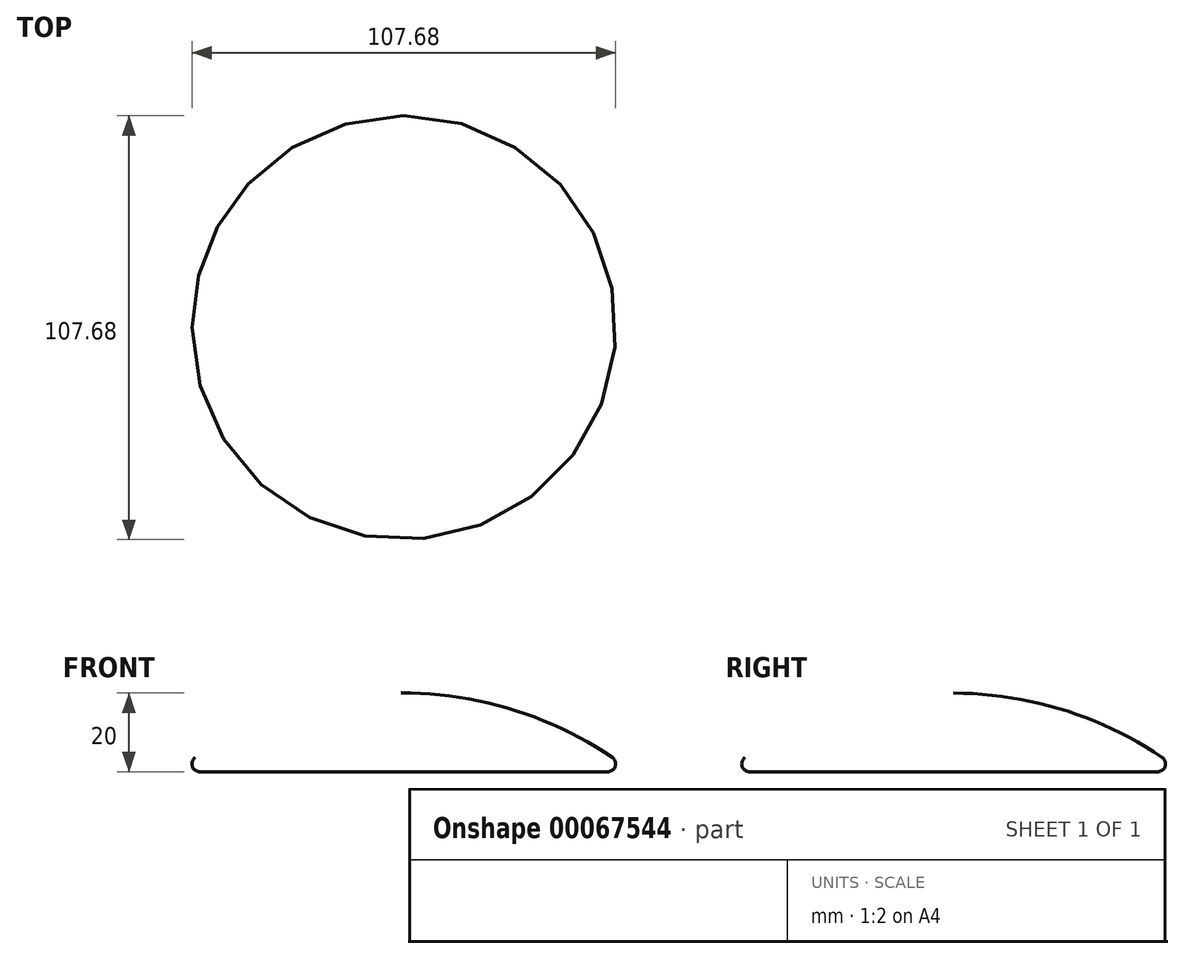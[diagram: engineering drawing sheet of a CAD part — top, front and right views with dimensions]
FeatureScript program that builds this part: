
annotation { "Feature Type Name" : "Feature", "Feature Type Description" : "" }
export const myFeature = defineFeature(function(context is Context, id is Id, definition is map)
    precondition{}
    {
        {
            var Q0;
            Q0=qCreatedBy(makeId("Front.planeOp"),FACE);
            var sketch = newSketch(context, id + "F0", { "sketchPlane" : qUnion([Q0])});
            skLineSegment(sketch, "E0", {"start": v(0, 0) * mm, "end": v(0, 20) * mm});
            skLineSegment(sketch, "E1", {"start": v(0, 0) * mm, "end": v(58, 0) * mm});
            skArc(sketch, "E2", {"start": v(58, 0) * mm, "mid": v(30.66, 14.8) * mm, "end": v(0, 20) * mm});
            skSolve(sketch);
        }
        {
            var Q0;
            Q0 = qSketchRegion(id + "F0", true);
            var Q1;
            Q1=sQuery(id+"F0.wireOp",EDGE,"E0");
            revolve(context, id + "F1", {"entities" : qUnion([Q0]), "axis" : qUnion([Q1]), "revolveType" : RevolveType.FULL});
        }
        {
            var Q0;
            Q0=makeQuery(id+"F1.opRevolve","SWEPT_FACE",FACE,{"disambiguationData":[OSD([sQuery(id+"F0.wireOp",EDGE,"E1")])]});
            fillet(context, id + "F2", {"entities" : qUnion([Q0]), "radius" : 2 * mm, "tangentPropagation" : true, "allowEdgeOverflow" : false});
        }
    });
